# Revit family: CCR
name_source: partatom
category: Lighting Fixtures
units: mm (PartAtom-declared; Revit-internal decimal feet)

## family parameters
Cut with Voids When Loaded = No
Host = Face
Light Source = Yes
OmniClass Number = 23.80.70.11.21
OmniClass Title = Emergency Lighting
Part Type = Normal
Room Calculation Point = No
Round Connector Dimension = Use Diameter
Shared = No

## types (7) — shared parameters
Color Filter = 16777215
Default Elevation = 48.000"
Dimming Lamp Color Temperature Shift = <None>
Emit Shape Visible in Rendering = No
Emit from Rectangle Length = 10.000"
Emit from Rectangle Width = 5.000"
Is 120VAC = Yes
Is 277VAC = No
Lamp = LED Lamp
Load Classification = Lighting
Manufacturer = Compass Products
Photometric Web File = generic
URL = https://www.currentlighting.com
Voltage = 120 V
zz Watts 1 = 3 W
zz Watts 2 = 4 W
zz Watts 3 = 4 W
zz Watts 4 = 3 W

## per-type parameters (varying)
| type | Apparent Load | Description | Finish | Lens | Model | Tilt Angle | Wattage Comments | Watts | zz Integer 1 |
| CCR | 3 VA | Black Thermoplastic, Combination Exit/Emergency Light, Universal Face, Green Letters | White | Green Glass | CCGB | 90.00° | 3.22 - 3.18 W | 3 W | 1 |
| CCRB | 4 VA | Black Thermoplastic, Combination Exit/Emergency Light, Universal Face, Red Letters | Black | Red Glass | CCRB | 0.00° | 4.12 - 3.20 W | 4 W | 2 |
| CCG | 3 VA | White Thermoplastic, Combination Exit/Emergency Light, Universal Face, Green Letters | White | Green Glass | CCG | 0.00° | 3.22 - 3.18 W | 3 W | 1 |
| CCGB | 3 VA | Black Thermoplastic, Combination Exit/Emergency Light, Universal Face, Green Letters | White | Green Glass | CCGB | 90.00° | 3.22 - 3.18 W | 3 W | 1 |
| CCRRC | 4 VA | White Thermoplastic, Combination Exit/Emergency Light, Universal Face, Red Letters, Remote Capacity | White | Red Glass | CCRRC | 0.00° | 3.56 - 4.06 W | 4 W | 3 |
| CCRRCB | 4 VA | Black Thermoplastic, Combination Exit/Emergency Light, Universal Face, Red Letters, Remote Capacity | Black | Red Glass | CCRRCB | 0.00° | 3.56 - 4.06 W | 4 W | 3 |
| CCGRC | 3 VA | White Thermoplastic, Combination Exit/Emergency Light, Universal Face, Green Letters, Remote Capacity | White | Green Glass | CCGRC | 0.00° | 3.20 - 3.80 W | 3 W | 4 |

## geometry (parser evidence)
native form markers: Blend x10, Sweep x6
no freeform markers — native parametric forms only
